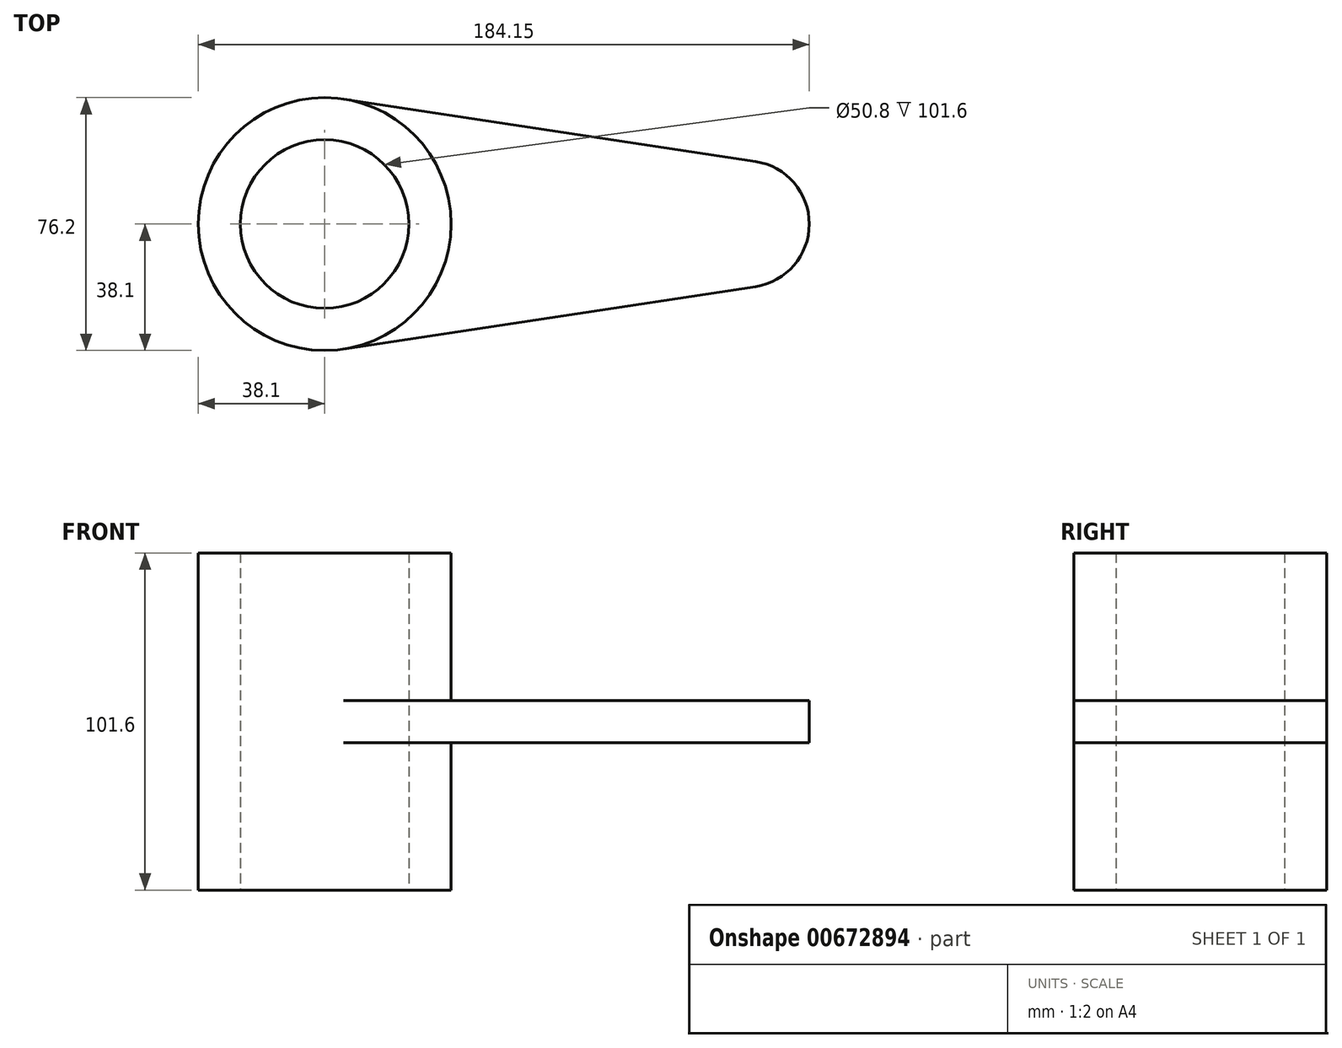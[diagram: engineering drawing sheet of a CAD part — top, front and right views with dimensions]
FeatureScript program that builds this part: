
annotation { "Feature Type Name" : "Feature", "Feature Type Description" : "" }
export const myFeature = defineFeature(function(context is Context, id is Id, definition is map)
    precondition{}
    {
        {
            var Q0;
            Q0=qCreatedBy(makeId("Top.planeOp"),FACE);
            var sketch = newSketch(context, id + "F0", { "sketchPlane" : qUnion([Q0])});
            skCircle(sketch, "E0", {"center": v(0, 0) * mm, "radius": 38.1 * mm});
            skCircle(sketch, "E1", {"center": v(0, 0) * mm, "radius": 25.4 * mm});
            skSolve(sketch);
        }
        {
            var Q0;
            Q0 = qSketchRegion(id + "F0", true);
            extrude(context, id + "F1", {"entities" : qUnion([Q0]), "depth" : 101.6 * mm, "offsetDistance" : 25.4 * mm});
        }
        {
            var Q0;
            Q0=qCreatedBy(makeId("Top.planeOp"),FACE);
            cPlane(context, id + "F2", {"entities" : qUnion([Q0]), "cplaneType" : CPlaneType.OFFSET, "offset" : 50.8 * mm, "width" : 152.4 * mm, "height" : 152.4 * mm});
        }
        {
            var Q0;
            Q0=qCreatedBy(id+"F2.planeOp",FACE);
            var sketch = newSketch(context, id + "F3", { "sketchPlane" : qUnion([Q0])});
            skCircle(sketch, "E2", {"center": v(0, 0) * mm, "radius": 38.1 * mm});
            skArc(sketch, "E3", {"start": v(129.86, -18.83) * mm, "mid": v(146.05, 0) * mm, "end": v(129.86, 18.83) * mm});
            skArc(sketch, "E4", {"start": v(5.72, 37.67) * mm, "mid": v(-38.1, 0) * mm, "end": v(5.72, -37.67) * mm});
            skLineSegment(sketch, "E5", {"start": v(5.71, 37.67) * mm, "end": v(129.86, 18.83) * mm});
            skLineSegment(sketch, "E6", {"start": v(5.71, -37.67) * mm, "end": v(129.86, -18.83) * mm});
            skCircle(sketch, "E7", {"center": v(0, 0) * mm, "radius": 25.4 * mm});
            skSolve(sketch);
        }
        {
            var Q0;
            Q0 = qSketchRegion(id + "F3", true);
            extrude(context, id + "F4", {"entities" : qUnion([Q0]), "operationType" : NewBodyOperationType.ADD, "endBound" : BoundingType.SYMMETRIC, "depth" : 12.7 * mm, "offsetDistance" : 25.4 * mm});
        }
    });
